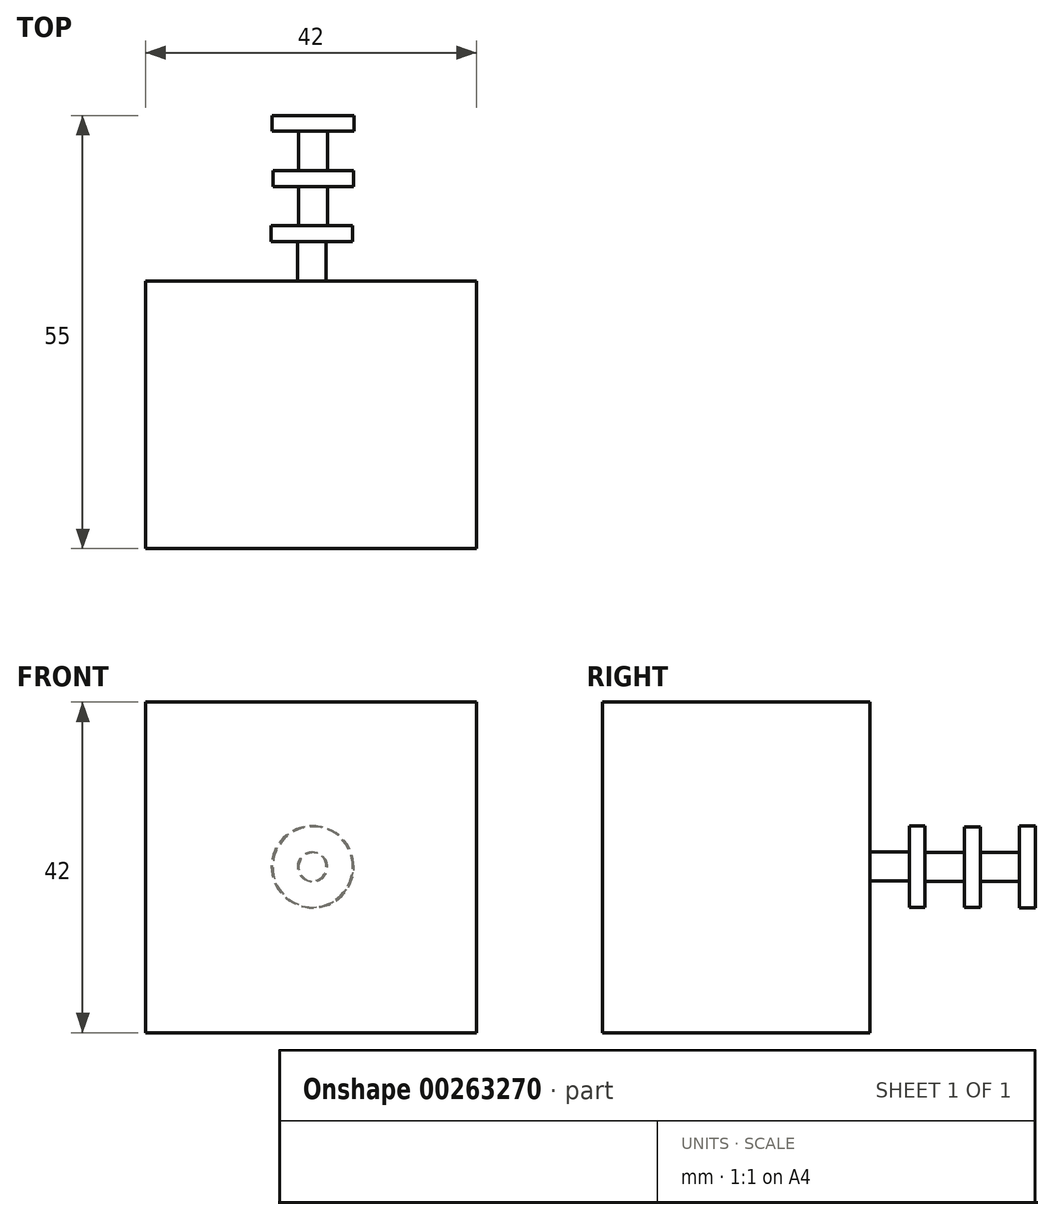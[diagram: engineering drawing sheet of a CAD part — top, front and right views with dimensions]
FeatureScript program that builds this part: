
annotation { "Feature Type Name" : "Feature", "Feature Type Description" : "" }
export const myFeature = defineFeature(function(context is Context, id is Id, definition is map)
    precondition{}
    {
        {
            var Q0;
            Q0=qCreatedBy(makeId("Front.planeOp"),FACE);
            var sketch = newSketch(context, id + "F0", { "sketchPlane" : qUnion([Q0])});
            skLineSegment(sketch, "E0.bottom", {"start": v(0, 0) * mm, "end": v(42, 0) * mm});
            skLineSegment(sketch, "E0.top", {"start": v(0, 42) * mm, "end": v(42, 42) * mm});
            skLineSegment(sketch, "E0.left", {"start": v(0, 0) * mm, "end": v(0, 42) * mm});
            skLineSegment(sketch, "E0.right", {"start": v(42, 0) * mm, "end": v(42, 42) * mm});
            skSolve(sketch);
        }
        {
            var Q0;
            Q0 = qSketchRegion(id + "F0", true);
            extrude(context, id + "F1", {"entities" : qUnion([Q0]), "depth" : 34 * mm});
        }
        {
            var Q0;
            Q0=makeQuery(id+"F0.imprint","IMPRINT",FACE,{"disambiguationData":[TD([[makeQuery(id+"F0.imprint","IMPRINT",EDGE,{"derivedFrom":sQuery(id+"F0.wireOp",EDGE,"E0.bottom")}),1.0]])]});
            var sketch = newSketch(context, id + "F2", { "sketchPlane" : qUnion([Q0])});
            skCircle(sketch, "E1", {"center": v(21.1, 21.1) * mm, "radius": 1.83 * mm});
            skSolve(sketch);
        }
        {
            var Q0;
            Q0 = qSketchRegion(id + "F2", true);
            extrude(context, id + "F3", {"entities" : qUnion([Q0]), "operationType" : NewBodyOperationType.ADD, "oppositeDirection" : true, "depth" : 5 * mm});
        }
        {
            var Q0;
            Q0=makeQuery(id+"F3.opExtrude","CAP_FACE",FACE,{"disambiguationData":[OSD([sQuery(id+"F2.wireOp",EDGE,"E1")])],"isStart":false});
            var sketch = newSketch(context, id + "F4", { "sketchPlane" : qUnion([Q0])});
            skCircle(sketch, "E2", {"center": v(-21.1, 21.1) * mm, "radius": 5.17 * mm});
            skSolve(sketch);
        }
        {
            var Q0;
            Q0 = qSketchRegion(id + "F4", true);
            extrude(context, id + "F5", {"entities" : qUnion([Q0]), "operationType" : NewBodyOperationType.ADD, "depth" : 2 * mm});
        }
        {
            var Q0;
            Q0=makeQuery(id+"F4.imprint","IMPRINT",FACE,{"disambiguationData":[TD([[makeQuery(id+"F4.imprint","IMPRINT",EDGE,{"derivedFrom":makeQuery(id+"F3.opExtrude","CAP_EDGE",EDGE,{"disambiguationData":[OSD([sQuery(id+"F2.wireOp",EDGE,"E1")])],"isStart":false})}),-1.0]])]});
            var sketch = newSketch(context, id + "F6", { "sketchPlane" : qUnion([Q0])});
            skCircle(sketch, "E3", {"center": v(-21.25, 21.05) * mm, "radius": 1.82 * mm});
            skSolve(sketch);
        }
        {
            var Q0;
            Q0 = qSketchRegion(id + "F6", true);
            extrude(context, id + "F7", {"entities" : qUnion([Q0]), "operationType" : NewBodyOperationType.ADD, "depth" : 7 * mm});
        }
        {
            var Q0;
            Q0=makeQuery(id+"F7.opExtrude","CAP_FACE",FACE,{"disambiguationData":[OSD([sQuery(id+"F6.wireOp",EDGE,"E3")])],"isStart":false});
            var sketch = newSketch(context, id + "F8", { "sketchPlane" : qUnion([Q0])});
            skCircle(sketch, "E4", {"center": v(-21.25, 21.05) * mm, "radius": 5.11 * mm});
            skSolve(sketch);
        }
        {
            var Q0;
            Q0 = qSketchRegion(id + "F8", true);
            extrude(context, id + "F9", {"entities" : qUnion([Q0]), "operationType" : NewBodyOperationType.ADD, "depth" : 2 * mm});
        }
        {
            var Q0;
            Q0=makeQuery(id+"F8.imprint","IMPRINT",FACE,{"disambiguationData":[TD([[makeQuery(id+"F8.imprint","IMPRINT",EDGE,{"derivedFrom":makeQuery(id+"F7.opExtrude","CAP_EDGE",EDGE,{"disambiguationData":[OSD([sQuery(id+"F6.wireOp",EDGE,"E3")])],"isStart":false})}),1.0]])]});
            var sketch = newSketch(context, id + "F10", { "sketchPlane" : qUnion([Q0])});
            skCircle(sketch, "E5", {"center": v(-21.25, 21.05) * mm, "radius": 1.84 * mm});
            skSolve(sketch);
        }
        {
            var Q0;
            Q0 = qSketchRegion(id + "F10", true);
            extrude(context, id + "F11", {"entities" : qUnion([Q0]), "operationType" : NewBodyOperationType.ADD, "depth" : 7 * mm});
        }
        {
            var Q0;
            Q0=makeQuery(id+"F11.opExtrude","CAP_FACE",FACE,{"disambiguationData":[OSD([sQuery(id+"F10.wireOp",EDGE,"E5")])],"isStart":false});
            var sketch = newSketch(context, id + "F12", { "sketchPlane" : qUnion([Q0])});
            skCircle(sketch, "E6", {"center": v(-21.25, 21.05) * mm, "radius": 5.2 * mm});
            skSolve(sketch);
        }
        {
            var Q0;
            Q0 = qSketchRegion(id + "F12", true);
            extrude(context, id + "F13", {"entities" : qUnion([Q0]), "operationType" : NewBodyOperationType.ADD, "depth" : 2 * mm});
        }
    });
